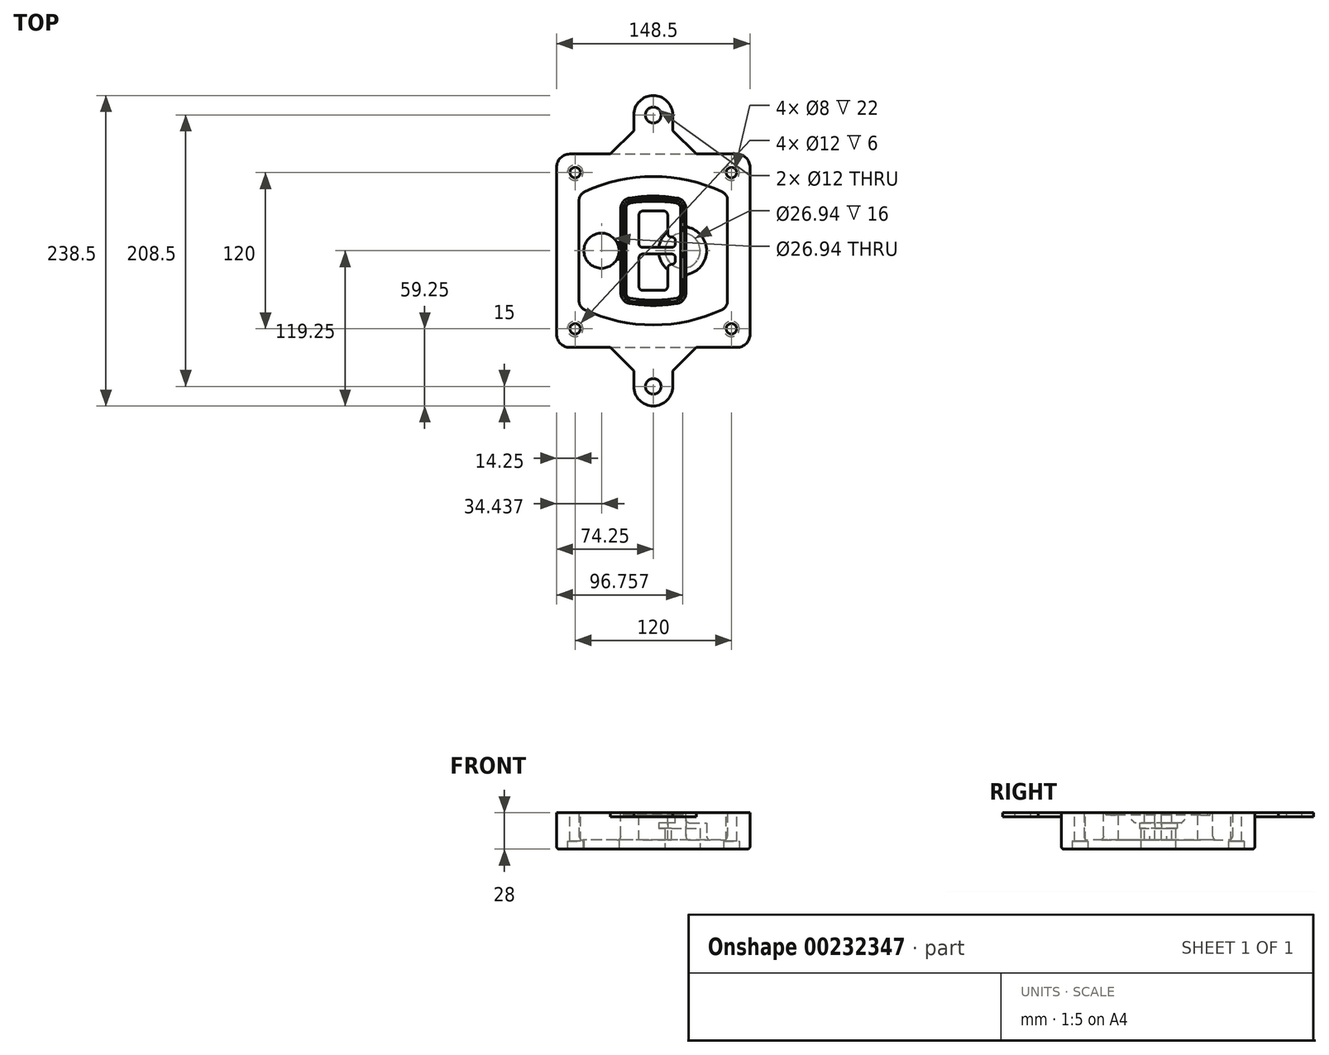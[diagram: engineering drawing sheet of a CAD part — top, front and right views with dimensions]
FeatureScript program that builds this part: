
annotation { "Feature Type Name" : "Feature", "Feature Type Description" : "" }
export const myFeature = defineFeature(function(context is Context, id is Id, definition is map)
    precondition{}
    {
        {
            var Q0;
            Q0=qCreatedBy(makeId("Top.planeOp"),FACE);
            var sketch = newSketch(context, id + "F0", { "sketchPlane" : qUnion([Q0])});
            skPoint(sketch, "E0.rect.middle", {"position": v(0, 0) * mm});
            skLineSegment(sketch, "E1.bottom", {"start": v(-64.25, -74.25) * mm, "end": v(64.25, -74.25) * mm});
            skLineSegment(sketch, "E1.top", {"start": v(-64.25, 74.25) * mm, "end": v(64.25, 74.25) * mm});
            skLineSegment(sketch, "E1.left", {"start": v(-74.25, -64.25) * mm, "end": v(-74.25, 64.25) * mm});
            skLineSegment(sketch, "E1.right", {"start": v(74.25, -64.25) * mm, "end": v(74.25, 64.25) * mm});
            skLineSegment(sketch, "E2", {"start": v(-74.25, 74.25) * mm, "end": v(74.25, -74.25) * mm, "construction": true});
            skLineSegment(sketch, "E3", {"start": v(74.25, 74.25) * mm, "end": v(-74.25, -74.25) * mm, "construction": true});
            skCircle(sketch, "E4", {"center": v(-60, 60) * mm, "radius": 4 * mm});
            skCircle(sketch, "E5", {"center": v(60, 60) * mm, "radius": 4 * mm});
            skCircle(sketch, "E6", {"center": v(60, -60) * mm, "radius": 4 * mm});
            skCircle(sketch, "E7", {"center": v(-60, -60) * mm, "radius": 4 * mm});
            skLineSegment(sketch, "E8", {"start": v(-60, 60) * mm, "end": v(60, 60) * mm, "construction": true});
            skLineSegment(sketch, "E9", {"start": v(60, 60) * mm, "end": v(60, -60) * mm, "construction": true});
            skLineSegment(sketch, "E10", {"start": v(60, -60) * mm, "end": v(-60, -60) * mm, "construction": true});
            skLineSegment(sketch, "E11", {"start": v(-60, -60) * mm, "end": v(-60, 60) * mm, "construction": true});
            skLineSegment(sketch, "E12", {"start": v(-60, 38.83) * mm, "end": v(-60, -38.83) * mm});
            skLineSegment(sketch, "E13", {"start": v(60, 38.83) * mm, "end": v(60, -38.83) * mm});
            skArc(sketch, "E14", {"start": v(54.26, 47.88) * mm, "mid": v(0, 60) * mm, "end": v(-54.26, 47.88) * mm});
            skArc(sketch, "E15", {"start": v(-54.26, -47.88) * mm, "mid": v(0, -60) * mm, "end": v(54.26, -47.88) * mm});
            skLineSegment(sketch, "E16", {"start": v(-60, 0) * mm, "end": v(60, 0) * mm, "construction": true});
            skPoint(sketch, "E17.visualSharp", {"position": v(-60, -45) * mm});
            skArc(sketch, "E17.filletArc", {"start": v(-60, -38.83) * mm, "mid": v(-58.44, -44.2) * mm, "end": v(-54.26, -47.88) * mm});
            skPoint(sketch, "E18.visualSharp", {"position": v(-60, 45) * mm});
            skArc(sketch, "E18.filletArc", {"start": v(-54.26, 47.88) * mm, "mid": v(-58.44, 44.2) * mm, "end": v(-60, 38.83) * mm});
            skPoint(sketch, "E19.visualSharp", {"position": v(60, 45) * mm});
            skArc(sketch, "E19.filletArc", {"start": v(60, 38.83) * mm, "mid": v(58.44, 44.2) * mm, "end": v(54.26, 47.88) * mm});
            skPoint(sketch, "E20.visualSharp", {"position": v(60, -45) * mm});
            skArc(sketch, "E20.filletArc", {"start": v(54.26, -47.88) * mm, "mid": v(58.44, -44.2) * mm, "end": v(60, -38.83) * mm});
            skPoint(sketch, "E21.visualSharp", {"position": v(-74.25, 74.25) * mm});
            skArc(sketch, "E21.filletArc", {"start": v(-64.25, 74.25) * mm, "mid": v(-71.32, 71.32) * mm, "end": v(-74.25, 64.25) * mm});
            skPoint(sketch, "E22.visualSharp", {"position": v(74.25, 74.25) * mm});
            skArc(sketch, "E22.filletArc", {"start": v(74.25, 64.25) * mm, "mid": v(71.32, 71.32) * mm, "end": v(64.25, 74.25) * mm});
            skPoint(sketch, "E23.visualSharp", {"position": v(74.25, -74.25) * mm});
            skArc(sketch, "E23.filletArc", {"start": v(64.25, -74.25) * mm, "mid": v(71.32, -71.32) * mm, "end": v(74.25, -64.25) * mm});
            skPoint(sketch, "E24.visualSharp", {"position": v(-74.25, -74.25) * mm});
            skArc(sketch, "E24.filletArc", {"start": v(-74.25, -64.25) * mm, "mid": v(-71.32, -71.32) * mm, "end": v(-64.25, -74.25) * mm});
            skArc(sketch, "E25.0", {"start": v(57, 38.83) * mm, "mid": v(55.9, 42.58) * mm, "end": v(52.98, 45.17) * mm});
            skLineSegment(sketch, "E25.1", {"start": v(57, 38.83) * mm, "end": v(57, -38.83) * mm});
            skArc(sketch, "E25.2", {"start": v(52.98, -45.17) * mm, "mid": v(55.9, -42.58) * mm, "end": v(57, -38.83) * mm});
            skArc(sketch, "E25.3", {"start": v(-52.98, -45.17) * mm, "mid": v(0, -57) * mm, "end": v(52.98, -45.17) * mm});
            skArc(sketch, "E25.4", {"start": v(-57, -38.83) * mm, "mid": v(-55.9, -42.58) * mm, "end": v(-52.98, -45.17) * mm});
            skArc(sketch, "E25.5", {"start": v(52.98, 45.17) * mm, "mid": v(0, 57) * mm, "end": v(-52.98, 45.17) * mm});
            skLineSegment(sketch, "E25.6", {"start": v(-57, 38.83) * mm, "end": v(-57, -38.83) * mm});
            skArc(sketch, "E25.7", {"start": v(-52.98, 45.17) * mm, "mid": v(-55.9, 42.58) * mm, "end": v(-57, 38.83) * mm});
            skArc(sketch, "E26.0", {"start": v(-55.96, 51.5) * mm, "mid": v(-61.82, 46.33) * mm, "end": v(-64, 38.83) * mm});
            skArc(sketch, "E26.1", {"start": v(55.96, 51.5) * mm, "mid": v(0, 64) * mm, "end": v(-55.96, 51.5) * mm});
            skArc(sketch, "E26.2", {"start": v(64, 38.83) * mm, "mid": v(61.82, 46.33) * mm, "end": v(55.96, 51.5) * mm});
            skLineSegment(sketch, "E26.3", {"start": v(64, 38.83) * mm, "end": v(64, -38.83) * mm});
            skArc(sketch, "E26.4", {"start": v(55.96, -51.5) * mm, "mid": v(61.82, -46.33) * mm, "end": v(64, -38.83) * mm});
            skLineSegment(sketch, "E26.5", {"start": v(-64, 38.83) * mm, "end": v(-64, -38.83) * mm});
            skArc(sketch, "E26.6", {"start": v(-55.96, -51.5) * mm, "mid": v(0, -64) * mm, "end": v(55.96, -51.5) * mm});
            skArc(sketch, "E26.7", {"start": v(-64, -38.83) * mm, "mid": v(-61.82, -46.33) * mm, "end": v(-55.96, -51.5) * mm});
            skSolve(sketch);
        }
        {
            var Q0;
            Q0=makeQuery(id+"F0.imprint","IMPRINT",FACE,{"disambiguationData":[TD([[makeQuery(id+"F0.imprint","IMPRINT",EDGE,{"derivedFrom":sQuery(id+"F0.wireOp",EDGE,"E1.bottom")}),1.0]])]});
            var Q1;
            Q1=makeQuery(id+"F0.imprint","IMPRINT",FACE,{"disambiguationData":[TD([[makeQuery(id+"F0.imprint","IMPRINT",EDGE,{"derivedFrom":sQuery(id+"F0.wireOp",EDGE,"E12")}),1.0]])]});
            var Q2;
            Q2=makeQuery(id+"F0.imprint","IMPRINT",FACE,{"disambiguationData":[TD([[makeQuery(id+"F0.imprint","IMPRINT",EDGE,{"derivedFrom":sQuery(id+"F0.wireOp",EDGE,"E25.0")}),1.0]])]});
            var Q3;
            Q3=makeQuery(id+"F0.imprint","IMPRINT",FACE,{"disambiguationData":[TD([[makeQuery(id+"F0.imprint","IMPRINT",EDGE,{"derivedFrom":sQuery(id+"F0.wireOp",EDGE,"E12")}),-1.0]])]});
            extrude(context, id + "F1", {"entities" : qUnion([Q0, Q1, Q2, Q3]), "oppositeDirection" : true, "depth" : 25 * mm});
        }
        {
            var Q0;
            Q0=makeQuery(id+"F0.imprint","IMPRINT",FACE,{"disambiguationData":[TD([[makeQuery(id+"F0.imprint","IMPRINT",EDGE,{"derivedFrom":sQuery(id+"F0.wireOp",EDGE,"E12")}),1.0]])]});
            extrude(context, id + "F2", {"entities" : qUnion([Q0]), "operationType" : NewBodyOperationType.ADD, "depth" : 3 * mm});
        }
        {
            var Q0;
            Q0=makeQuery(id+"F0.imprint","IMPRINT",FACE,{"disambiguationData":[TD([[makeQuery(id+"F0.imprint","IMPRINT",EDGE,{"derivedFrom":sQuery(id+"F0.wireOp",EDGE,"E25.0")}),1.0]])]});
            extrude(context, id + "F3", {"entities" : qUnion([Q0]), "operationType" : NewBodyOperationType.REMOVE, "oppositeDirection" : true, "depth" : 18 * mm});
        }
        {
            var Q0;
            Q0=makeQuery(id+"F2.opExtrude","CAP_FACE",FACE,{"disambiguationData":[OSD([sQuery(id+"F0.wireOp",EDGE,"E12"),sQuery(id+"F0.wireOp",EDGE,"E13"),sQuery(id+"F0.wireOp",EDGE,"E14"),sQuery(id+"F0.wireOp",EDGE,"E15"),sQuery(id+"F0.wireOp",EDGE,"E17.filletArc"),sQuery(id+"F0.wireOp",EDGE,"E18.filletArc"),sQuery(id+"F0.wireOp",EDGE,"E19.filletArc"),sQuery(id+"F0.wireOp",EDGE,"E20.filletArc"),sQuery(id+"F0.wireOp",EDGE,"E25.0"),sQuery(id+"F0.wireOp",EDGE,"E25.1"),sQuery(id+"F0.wireOp",EDGE,"E25.2"),sQuery(id+"F0.wireOp",EDGE,"E25.3"),sQuery(id+"F0.wireOp",EDGE,"E25.4"),sQuery(id+"F0.wireOp",EDGE,"E25.5"),sQuery(id+"F0.wireOp",EDGE,"E25.6"),sQuery(id+"F0.wireOp",EDGE,"E25.7")])],"isStart":false});
            var sketch = newSketch(context, id + "F4", { "sketchPlane" : qUnion([Q0])});
            skArc(sketch, "E27.0", {"start": v(-18.34, -40.45) * mm, "mid": v(0, -42) * mm, "end": v(18.34, -40.45) * mm});
            skArc(sketch, "E28.0", {"start": v(18.34, 40.45) * mm, "mid": v(0, 42) * mm, "end": v(-18.34, 40.45) * mm});
            skLineSegment(sketch, "E29", {"start": v(-25, 32.57) * mm, "end": v(-25, -32.57) * mm});
            skLineSegment(sketch, "E30", {"start": v(25, 32.57) * mm, "end": v(25, -32.57) * mm});
            skLineSegment(sketch, "E31", {"start": v(-25, 39.1) * mm, "end": v(25, 39.1) * mm, "construction": true});
            skLineSegment(sketch, "E32", {"start": v(-25, -39.1) * mm, "end": v(25, -39.1) * mm, "construction": true});
            skPoint(sketch, "E33.visualSharp", {"position": v(-25, 39.1) * mm});
            skArc(sketch, "E33.filletArc", {"start": v(-18.34, 40.45) * mm, "mid": v(-23.11, 37.73) * mm, "end": v(-25, 32.57) * mm});
            skPoint(sketch, "E34.visualSharp", {"position": v(25, 39.1) * mm});
            skArc(sketch, "E34.filletArc", {"start": v(25, 32.57) * mm, "mid": v(23.11, 37.73) * mm, "end": v(18.34, 40.45) * mm});
            skPoint(sketch, "E35.visualSharp", {"position": v(25, -39.1) * mm});
            skArc(sketch, "E35.filletArc", {"start": v(18.34, -40.45) * mm, "mid": v(23.11, -37.73) * mm, "end": v(25, -32.57) * mm});
            skPoint(sketch, "E36.visualSharp", {"position": v(-25, -39.1) * mm});
            skArc(sketch, "E36.filletArc", {"start": v(-25, -32.57) * mm, "mid": v(-23.11, -37.73) * mm, "end": v(-18.34, -40.45) * mm});
            skArc(sketch, "E37.0", {"start": v(52.98, 45.17) * mm, "mid": v(0, 57) * mm, "end": v(-52.98, 45.17) * mm});
            skArc(sketch, "E37.1", {"start": v(-52.98, 45.17) * mm, "mid": v(-55.9, 42.58) * mm, "end": v(-57, 38.83) * mm});
            skLineSegment(sketch, "E37.2", {"start": v(-57, 38.83) * mm, "end": v(-57, -38.83) * mm});
            skArc(sketch, "E37.3", {"start": v(-57, -38.83) * mm, "mid": v(-55.9, -42.58) * mm, "end": v(-52.98, -45.17) * mm});
            skArc(sketch, "E37.4", {"start": v(-52.98, -45.17) * mm, "mid": v(0, -57) * mm, "end": v(52.98, -45.17) * mm});
            skArc(sketch, "E37.5", {"start": v(52.98, -45.17) * mm, "mid": v(55.9, -42.58) * mm, "end": v(57, -38.83) * mm});
            skLineSegment(sketch, "E37.6", {"start": v(57, 38.83) * mm, "end": v(57, -38.83) * mm});
            skArc(sketch, "E37.7", {"start": v(57, 38.83) * mm, "mid": v(55.9, 42.58) * mm, "end": v(52.98, 45.17) * mm});
            skLineSegment(sketch, "E38.0", {"start": v(23, 32.57) * mm, "end": v(23, -32.57) * mm});
            skArc(sketch, "E38.1", {"start": v(18, -38.48) * mm, "mid": v(21.58, -36.44) * mm, "end": v(23, -32.57) * mm});
            skArc(sketch, "E38.2", {"start": v(-18, -38.48) * mm, "mid": v(0, -40) * mm, "end": v(18, -38.48) * mm});
            skArc(sketch, "E38.3", {"start": v(-23, -32.57) * mm, "mid": v(-21.58, -36.44) * mm, "end": v(-18, -38.48) * mm});
            skLineSegment(sketch, "E38.4", {"start": v(-23, 32.57) * mm, "end": v(-23, -32.57) * mm});
            skArc(sketch, "E38.5", {"start": v(23, 32.57) * mm, "mid": v(21.58, 36.44) * mm, "end": v(18, 38.48) * mm});
            skArc(sketch, "E38.6", {"start": v(-18, 38.48) * mm, "mid": v(-21.58, 36.44) * mm, "end": v(-23, 32.57) * mm});
            skArc(sketch, "E38.7", {"start": v(18, 38.48) * mm, "mid": v(0, 40) * mm, "end": v(-18, 38.48) * mm});
            skArc(sketch, "E39.0", {"start": v(21, 32.57) * mm, "mid": v(20.06, 35.15) * mm, "end": v(17.67, 36.5) * mm});
            skLineSegment(sketch, "E39.1", {"start": v(21, 32.57) * mm, "end": v(21, -32.57) * mm});
            skArc(sketch, "E39.2", {"start": v(17.67, -36.5) * mm, "mid": v(20.06, -35.15) * mm, "end": v(21, -32.57) * mm});
            skArc(sketch, "E39.3", {"start": v(-17.67, -36.5) * mm, "mid": v(0, -38) * mm, "end": v(17.67, -36.5) * mm});
            skArc(sketch, "E39.4", {"start": v(-21, -32.57) * mm, "mid": v(-20.06, -35.15) * mm, "end": v(-17.67, -36.5) * mm});
            skArc(sketch, "E39.5", {"start": v(17.67, 36.5) * mm, "mid": v(0, 38) * mm, "end": v(-17.67, 36.5) * mm});
            skLineSegment(sketch, "E39.6", {"start": v(-21, 32.57) * mm, "end": v(-21, -32.57) * mm});
            skArc(sketch, "E39.7", {"start": v(-17.67, 36.5) * mm, "mid": v(-20.06, 35.15) * mm, "end": v(-21, 32.57) * mm});
            skLineSegment(sketch, "E40", {"start": v(-25, 0) * mm, "end": v(25, 0) * mm, "construction": true});
            skLineSegment(sketch, "E41", {"start": v(-11, 5.5) * mm, "end": v(-11, 27.5) * mm});
            skLineSegment(sketch, "E42", {"start": v(-8, 30.5) * mm, "end": v(8, 30.5) * mm});
            skLineSegment(sketch, "E43", {"start": v(11, 27.5) * mm, "end": v(11, 13.5) * mm});
            skLineSegment(sketch, "E44", {"start": v(14, 10.5) * mm, "end": v(14, 10.5) * mm});
            skLineSegment(sketch, "E45", {"start": v(17, 7.5) * mm, "end": v(17, 5.5) * mm});
            skLineSegment(sketch, "E46", {"start": v(14, 2.5) * mm, "end": v(-8, 2.5) * mm});
            skPoint(sketch, "E47.visualSharp", {"position": v(-11, 30.5) * mm});
            skArc(sketch, "E47.filletArc", {"start": v(-8, 30.5) * mm, "mid": v(-10.12, 29.62) * mm, "end": v(-11, 27.5) * mm});
            skPoint(sketch, "E48.visualSharp", {"position": v(11, 30.5) * mm});
            skArc(sketch, "E48.filletArc", {"start": v(11, 27.5) * mm, "mid": v(10.12, 29.62) * mm, "end": v(8, 30.5) * mm});
            skPoint(sketch, "E49.visualSharp", {"position": v(11, 10.5) * mm});
            skArc(sketch, "E49.filletArc", {"start": v(11, 13.5) * mm, "mid": v(11.88, 11.38) * mm, "end": v(14, 10.5) * mm});
            skPoint(sketch, "E50.visualSharp", {"position": v(17, 10.5) * mm});
            skArc(sketch, "E50.filletArc", {"start": v(17, 7.5) * mm, "mid": v(16.12, 9.62) * mm, "end": v(14, 10.5) * mm});
            skPoint(sketch, "E51.visualSharp", {"position": v(17, 2.5) * mm});
            skArc(sketch, "E51.filletArc", {"start": v(14, 2.5) * mm, "mid": v(16.12, 3.38) * mm, "end": v(17, 5.5) * mm});
            skPoint(sketch, "E52.visualSharp", {"position": v(-11, 2.5) * mm});
            skArc(sketch, "E52.filletArc", {"start": v(-11, 5.5) * mm, "mid": v(-10.12, 3.38) * mm, "end": v(-8, 2.5) * mm});
            skLineSegment(sketch, "E53.0.MirrorCS", {"start": v(14, -2.5) * mm, "end": v(-8, -2.5) * mm});
            skArc(sketch, "E54.0.MirrorCS", {"start": v(-11, -5.5) * mm, "mid": v(-10.12, -3.38) * mm, "end": v(-8, -2.5) * mm});
            skLineSegment(sketch, "E55.0.MirrorCS", {"start": v(-11, -5.5) * mm, "end": v(-11, -27.5) * mm});
            skArc(sketch, "E56.0.MirrorCS", {"start": v(-8, -30.5) * mm, "mid": v(-10.12, -29.62) * mm, "end": v(-11, -27.5) * mm});
            skLineSegment(sketch, "E57.0.MirrorCS", {"start": v(-8, -30.5) * mm, "end": v(8, -30.5) * mm});
            skArc(sketch, "E58.0.MirrorCS", {"start": v(11, -27.5) * mm, "mid": v(10.12, -29.62) * mm, "end": v(8, -30.5) * mm});
            skLineSegment(sketch, "E59.0.MirrorCS", {"start": v(11, -27.5) * mm, "end": v(11, -13.5) * mm});
            skArc(sketch, "E60.0.MirrorCS", {"start": v(11, -13.5) * mm, "mid": v(11.88, -11.38) * mm, "end": v(14, -10.5) * mm});
            skArc(sketch, "E61.0.MirrorCS", {"start": v(17, -7.5) * mm, "mid": v(16.12, -9.62) * mm, "end": v(14, -10.5) * mm});
            skLineSegment(sketch, "E62.0.MirrorCS", {"start": v(17, -7.5) * mm, "end": v(17, -5.5) * mm});
            skArc(sketch, "E63.0.MirrorCS", {"start": v(14, -2.5) * mm, "mid": v(16.12, -3.38) * mm, "end": v(17, -5.5) * mm});
            skSolve(sketch);
        }
        {
            var Q0;
            Q0=makeQuery(id+"F4.imprint","IMPRINT",FACE,{"disambiguationData":[TD([[makeQuery(id+"F4.imprint","IMPRINT",EDGE,{"derivedFrom":sQuery(id+"F4.wireOp",EDGE,"E27.0")}),1.0]])]});
            var Q1;
            Q1=makeQuery(id+"F4.imprint","IMPRINT",FACE,{"disambiguationData":[TD([[makeQuery(id+"F4.imprint","IMPRINT",EDGE,{"derivedFrom":sQuery(id+"F4.wireOp",EDGE,"E38.0")}),-1.0]])]});
            var Q2;
            Q2=makeQuery(id+"F4.imprint","IMPRINT",FACE,{"disambiguationData":[TD([[makeQuery(id+"F4.imprint","IMPRINT",EDGE,{"derivedFrom":sQuery(id+"F4.wireOp",EDGE,"E39.0")}),1.0]])]});
            extrude(context, id + "F5", {"entities" : qUnion([Q0, Q1, Q2]), "operationType" : NewBodyOperationType.ADD, "endBound" : BoundingType.UP_TO_NEXT, "oppositeDirection" : true, "depth" : 25 * mm});
        }
        {
            var Q0;
            Q0=makeQuery(id+"F4.imprint","IMPRINT",FACE,{"disambiguationData":[TD([[makeQuery(id+"F4.imprint","IMPRINT",EDGE,{"derivedFrom":sQuery(id+"F4.wireOp",EDGE,"E38.0")}),-1.0]])]});
            extrude(context, id + "F6", {"entities" : qUnion([Q0]), "operationType" : NewBodyOperationType.REMOVE, "oppositeDirection" : true, "depth" : 2 * mm});
        }
        {
            var Q0;
            Q0=makeQuery(id+"F1.opExtrude","CAP_FACE",FACE,{"disambiguationData":[OSD([sQuery(id+"F0.wireOp",EDGE,"E1.bottom"),sQuery(id+"F0.wireOp",EDGE,"E1.top"),sQuery(id+"F0.wireOp",EDGE,"E1.left"),sQuery(id+"F0.wireOp",EDGE,"E1.right"),sQuery(id+"F0.wireOp",EDGE,"E4"),sQuery(id+"F0.wireOp",EDGE,"E5"),sQuery(id+"F0.wireOp",EDGE,"E6"),sQuery(id+"F0.wireOp",EDGE,"E7"),sQuery(id+"F0.wireOp",EDGE,"E21.filletArc"),sQuery(id+"F0.wireOp",EDGE,"E22.filletArc"),sQuery(id+"F0.wireOp",EDGE,"E23.filletArc"),sQuery(id+"F0.wireOp",EDGE,"E24.filletArc")])],"isStart":false});
            var sketch = newSketch(context, id + "F7", { "sketchPlane" : qUnion([Q0])});
            skCircle(sketch, "E64", {"center": v(22.5, 0) * mm, "radius": 13.47 * mm});
            skCircle(sketch, "E65", {"center": v(-39.81, 0) * mm, "radius": 13.47 * mm});
            skLineSegment(sketch, "E66", {"start": v(74.25, 0) * mm, "end": v(-74.25, 0) * mm});
            skCircle(sketch, "E67", {"center": v(22.5, 0) * mm, "radius": 18.47 * mm});
            skCircle(sketch, "E68", {"center": v(60, -60) * mm, "radius": 6 * mm});
            skCircle(sketch, "E69", {"center": v(-60, -60) * mm, "radius": 6 * mm});
            skCircle(sketch, "E70", {"center": v(-60, 60) * mm, "radius": 6 * mm});
            skCircle(sketch, "E71", {"center": v(60, 60) * mm, "radius": 6 * mm});
            skSolve(sketch);
        }
        {
            var Q0;
            {var subQ1=sQuery(id+"F7.wireOp",EDGE,"E66");var subQ4=sQuery(id+"F7.wireOp",EDGE,"E64");var subQ6=makeQuery(id+"F7.imprint","INTERSECT",VERTEX,{"disambiguationData":[OD(0.0)],"derivedFrom":[subQ4,subQ1]});Q0=makeQuery(id+"F7.imprint","IMPRINT",FACE,{"disambiguationData":[TD([[makeQuery(id+"F7.imprint","IMPRINT",EDGE,{"disambiguationData":[TD([[subQ6,-1.0]])],"derivedFrom":subQ4}),-1.0]])]});}
            var Q1;
            {var subQ0=sQuery(id+"F7.wireOp",EDGE,"E66");var subQ1=sQuery(id+"F7.wireOp",EDGE,"E64");var subQ3=makeQuery(id+"F7.imprint","INTERSECT",VERTEX,{"disambiguationData":[OD(0.0)],"derivedFrom":[subQ1,subQ0]});Q1=makeQuery(id+"F7.imprint","IMPRINT",FACE,{"disambiguationData":[TD([[makeQuery(id+"F7.imprint","IMPRINT",EDGE,{"disambiguationData":[TD([[subQ3,-1.0]])],"derivedFrom":subQ1}),1.0]])]});}
            var Q2;
            {var subQ0=sQuery(id+"F7.wireOp",EDGE,"E66");var subQ1=sQuery(id+"F7.wireOp",EDGE,"E64");var subQ3=makeQuery(id+"F7.imprint","INTERSECT",VERTEX,{"disambiguationData":[OD(0.0)],"derivedFrom":[subQ1,subQ0]});Q2=makeQuery(id+"F7.imprint","IMPRINT",FACE,{"disambiguationData":[TD([[makeQuery(id+"F7.imprint","IMPRINT",EDGE,{"disambiguationData":[TD([[subQ3,1.0]])],"derivedFrom":subQ1}),1.0]])]});}
            var Q3;
            {var subQ1=sQuery(id+"F7.wireOp",EDGE,"E66");var subQ4=sQuery(id+"F7.wireOp",EDGE,"E64");var subQ6=makeQuery(id+"F7.imprint","INTERSECT",VERTEX,{"disambiguationData":[OD(0.0)],"derivedFrom":[subQ4,subQ1]});Q3=makeQuery(id+"F7.imprint","IMPRINT",FACE,{"disambiguationData":[TD([[makeQuery(id+"F7.imprint","IMPRINT",EDGE,{"disambiguationData":[TD([[subQ6,1.0]])],"derivedFrom":subQ4}),-1.0]])]});}
            extrude(context, id + "F8", {"entities" : qUnion([Q0, Q1, Q2, Q3]), "operationType" : NewBodyOperationType.ADD, "oppositeDirection" : true, "depth" : 20 * mm});
        }
        {
            var Q0;
            {var subQ0=sQuery(id+"F7.wireOp",EDGE,"E66");var subQ1=sQuery(id+"F7.wireOp",EDGE,"E64");var subQ3=makeQuery(id+"F7.imprint","INTERSECT",VERTEX,{"disambiguationData":[OD(0.0)],"derivedFrom":[subQ1,subQ0]});Q0=makeQuery(id+"F7.imprint","IMPRINT",FACE,{"disambiguationData":[TD([[makeQuery(id+"F7.imprint","IMPRINT",EDGE,{"disambiguationData":[TD([[subQ3,-1.0]])],"derivedFrom":subQ1}),1.0]])]});}
            var Q1;
            {var subQ0=sQuery(id+"F7.wireOp",EDGE,"E66");var subQ1=sQuery(id+"F7.wireOp",EDGE,"E64");var subQ3=makeQuery(id+"F7.imprint","INTERSECT",VERTEX,{"disambiguationData":[OD(0.0)],"derivedFrom":[subQ1,subQ0]});Q1=makeQuery(id+"F7.imprint","IMPRINT",FACE,{"disambiguationData":[TD([[makeQuery(id+"F7.imprint","IMPRINT",EDGE,{"disambiguationData":[TD([[subQ3,1.0]])],"derivedFrom":subQ1}),1.0]])]});}
            extrude(context, id + "F9", {"entities" : qUnion([Q0, Q1]), "operationType" : NewBodyOperationType.REMOVE, "oppositeDirection" : true, "depth" : 16 * mm});
        }
        {
            var Q0;
            {var subQ0=sQuery(id+"F7.wireOp",EDGE,"E66");var subQ1=sQuery(id+"F7.wireOp",EDGE,"E65");var subQ3=makeQuery(id+"F7.imprint","INTERSECT",VERTEX,{"disambiguationData":[OD(0.0)],"derivedFrom":[subQ1,subQ0]});Q0=makeQuery(id+"F7.imprint","IMPRINT",FACE,{"disambiguationData":[TD([[makeQuery(id+"F7.imprint","IMPRINT",EDGE,{"disambiguationData":[TD([[subQ3,-1.0]])],"derivedFrom":subQ1}),1.0]])]});}
            var Q1;
            {var subQ0=sQuery(id+"F7.wireOp",EDGE,"E66");var subQ1=sQuery(id+"F7.wireOp",EDGE,"E65");var subQ3=makeQuery(id+"F7.imprint","INTERSECT",VERTEX,{"disambiguationData":[OD(0.0)],"derivedFrom":[subQ1,subQ0]});Q1=makeQuery(id+"F7.imprint","IMPRINT",FACE,{"disambiguationData":[TD([[makeQuery(id+"F7.imprint","IMPRINT",EDGE,{"disambiguationData":[TD([[subQ3,1.0]])],"derivedFrom":subQ1}),1.0]])]});}
            extrude(context, id + "F10", {"entities" : qUnion([Q0, Q1]), "operationType" : NewBodyOperationType.REMOVE, "oppositeDirection" : true, "depth" : 25 * mm});
        }
        {
            var Q0;
            Q0=makeQuery(id+"F7.imprint","IMPRINT",FACE,{"disambiguationData":[TD([[makeQuery(id+"F7.imprint","IMPRINT",EDGE,{"derivedFrom":sQuery(id+"F7.wireOp",EDGE,"E68")}),1.0]])]});
            var Q1;
            Q1=makeQuery(id+"F7.imprint","IMPRINT",FACE,{"disambiguationData":[TD([[makeQuery(id+"F7.imprint","IMPRINT",EDGE,{"derivedFrom":makeQuery(id+"F1.opExtrude","CAP_EDGE",EDGE,{"disambiguationData":[OSD([sQuery(id+"F0.wireOp",EDGE,"E5")])],"isStart":false})}),-1.0]])]});
            var Q2;
            Q2=makeQuery(id+"F7.imprint","IMPRINT",FACE,{"disambiguationData":[TD([[makeQuery(id+"F7.imprint","IMPRINT",EDGE,{"derivedFrom":sQuery(id+"F7.wireOp",EDGE,"E69")}),1.0]])]});
            var Q3;
            Q3=makeQuery(id+"F7.imprint","IMPRINT",FACE,{"disambiguationData":[TD([[makeQuery(id+"F7.imprint","IMPRINT",EDGE,{"derivedFrom":makeQuery(id+"F1.opExtrude","CAP_EDGE",EDGE,{"disambiguationData":[OSD([sQuery(id+"F0.wireOp",EDGE,"E4")])],"isStart":false})}),-1.0]])]});
            var Q4;
            Q4=makeQuery(id+"F7.imprint","IMPRINT",FACE,{"disambiguationData":[TD([[makeQuery(id+"F7.imprint","IMPRINT",EDGE,{"derivedFrom":sQuery(id+"F7.wireOp",EDGE,"E70")}),1.0]])]});
            var Q5;
            Q5=makeQuery(id+"F7.imprint","IMPRINT",FACE,{"disambiguationData":[TD([[makeQuery(id+"F7.imprint","IMPRINT",EDGE,{"derivedFrom":makeQuery(id+"F1.opExtrude","CAP_EDGE",EDGE,{"disambiguationData":[OSD([sQuery(id+"F0.wireOp",EDGE,"E7")])],"isStart":false})}),-1.0]])]});
            var Q6;
            Q6=makeQuery(id+"F7.imprint","IMPRINT",FACE,{"disambiguationData":[TD([[makeQuery(id+"F7.imprint","IMPRINT",EDGE,{"derivedFrom":sQuery(id+"F7.wireOp",EDGE,"E71")}),1.0]])]});
            var Q7;
            Q7=makeQuery(id+"F7.imprint","IMPRINT",FACE,{"disambiguationData":[TD([[makeQuery(id+"F7.imprint","IMPRINT",EDGE,{"derivedFrom":makeQuery(id+"F1.opExtrude","CAP_EDGE",EDGE,{"disambiguationData":[OSD([sQuery(id+"F0.wireOp",EDGE,"E6")])],"isStart":false})}),-1.0]])]});
            extrude(context, id + "F11", {"entities" : qUnion([Q0, Q1, Q2, Q3, Q4, Q5, Q6, Q7]), "operationType" : NewBodyOperationType.REMOVE, "oppositeDirection" : true, "depth" : 6 * mm});
        }
        {
            var Q0;
            Q0=makeQuery(id+"F9.boolean.opBoolean","COPY",FACE,{"derivedFrom":makeQuery(id+"F9.opExtrude","CAP_FACE",FACE,{"disambiguationData":[OSD([sQuery(id+"F7.wireOp",EDGE,"E64")])],"isStart":false})});
            var sketch = newSketch(context, id + "F12", { "sketchPlane" : qUnion([Q0])});
            skArc(sketch, "E72.0", {"start": v(11, 14.45) * mm, "mid": v(6.45, 9.13) * mm, "end": v(4.2, 2.5) * mm});
            skArc(sketch, "E72.1", {"start": v(4.2, -2.5) * mm, "mid": v(6.45, -9.13) * mm, "end": v(11, -14.45) * mm});
            skLineSegment(sketch, "E73", {"start": v(4.2, -2.5) * mm, "end": v(14, -2.5) * mm});
            skLineSegment(sketch, "E74.0", {"start": v(14, 2.5) * mm, "end": v(4.2, 2.5) * mm});
            skArc(sketch, "E74.1", {"start": v(14, 2.5) * mm, "mid": v(16.12, 3.38) * mm, "end": v(17, 5.5) * mm});
            skLineSegment(sketch, "E74.2", {"start": v(17, 7.5) * mm, "end": v(17, 5.5) * mm});
            skArc(sketch, "E74.3", {"start": v(17, 7.5) * mm, "mid": v(16.12, 9.62) * mm, "end": v(14, 10.5) * mm});
            skArc(sketch, "E74.4", {"start": v(11, 13.5) * mm, "mid": v(11.88, 11.38) * mm, "end": v(14, 10.5) * mm});
            skLineSegment(sketch, "E74.5", {"start": v(11, 14.45) * mm, "end": v(11, 13.5) * mm});
            skLineSegment(sketch, "E74.7", {"start": v(14, -2.5) * mm, "end": v(4.2, -2.5) * mm});
            skArc(sketch, "E74.8", {"start": v(14, -2.5) * mm, "mid": v(16.12, -3.38) * mm, "end": v(17, -5.5) * mm});
            skLineSegment(sketch, "E74.9", {"start": v(17, -7.5) * mm, "end": v(17, -5.5) * mm});
            skArc(sketch, "E74.10", {"start": v(17, -7.5) * mm, "mid": v(16.12, -9.62) * mm, "end": v(14, -10.5) * mm});
            skArc(sketch, "E74.11", {"start": v(11, -13.5) * mm, "mid": v(11.88, -11.38) * mm, "end": v(14, -10.5) * mm});
            skLineSegment(sketch, "E74.12", {"start": v(11, -14.45) * mm, "end": v(11, -13.5) * mm});
            skPoint(sketch, "E75.orphan", {"position": v(11, -27.5) * mm});
            skPoint(sketch, "E76.orphan", {"position": v(-8, -2.5) * mm});
            skPoint(sketch, "E77.orphan", {"position": v(-8, 2.5) * mm});
            skPoint(sketch, "E78.orphan", {"position": v(11, 27.5) * mm});
            skSolve(sketch);
        }
        {
            var Q0;
            {var subQ7=sQuery(id+"F12.wireOp",EDGE,"E72.0");var subQ14=sQuery(id+"F12.wireOp",EDGE,"E72.1");var subQ16=sQuery(id+"F12.wireOp",EDGE,"E74.1");var subQ18=sQuery(id+"F12.wireOp",EDGE,"E74.8");Q0=qUnion([makeQuery(id+"F12.imprint","IMPRINT",FACE,{"disambiguationData":[TD([[makeQuery(id+"F12.imprint","IMPRINT",EDGE,{"derivedFrom":subQ7}),1.0]])]}),makeQuery(id+"F12.imprint","IMPRINT",FACE,{"disambiguationData":[TD([[makeQuery(id+"F12.imprint","IMPRINT",EDGE,{"derivedFrom":subQ14}),1.0]])]}),makeQuery(id+"F12.imprint","IMPRINT",FACE,{"disambiguationData":[TD([[makeQuery(id+"F12.imprint","IMPRINT",EDGE,{"derivedFrom":subQ16}),1.0]])]}),makeQuery(id+"F12.imprint","IMPRINT",FACE,{"disambiguationData":[TD([[makeQuery(id+"F12.imprint","IMPRINT",EDGE,{"derivedFrom":subQ18}),-1.0]])]})]);}
            var Q1;
            Q1=makeQuery(id+"F5.boolean.opBoolean","SPLIT",FACE,{"disambiguationData":[TD([makeQuery(id+"F5.opExtrude","SWEPT_FACE",FACE,{"disambiguationData":[OSD([sQuery(id+"F4.wireOp",EDGE,"E41")])]})])],"derivedFrom":makeQuery(id+"F3.boolean.opBoolean","COPY",FACE,{"derivedFrom":makeQuery(id+"F3.opExtrude","CAP_FACE",FACE,{"disambiguationData":[OSD([sQuery(id+"F0.wireOp",EDGE,"E25.0"),sQuery(id+"F0.wireOp",EDGE,"E25.1"),sQuery(id+"F0.wireOp",EDGE,"E25.2"),sQuery(id+"F0.wireOp",EDGE,"E25.3"),sQuery(id+"F0.wireOp",EDGE,"E25.4"),sQuery(id+"F0.wireOp",EDGE,"E25.5"),sQuery(id+"F0.wireOp",EDGE,"E25.6"),sQuery(id+"F0.wireOp",EDGE,"E25.7")])],"isStart":false})})});
            extrude(context, id + "F13", {"entities" : qUnion([Q0]), "operationType" : NewBodyOperationType.REMOVE, "endBound" : BoundingType.UP_TO_SURFACE, "endBoundEntityFace" : qUnion([Q1]), "depth" : 25 * mm});
        }
        {
            var Q0;
            Q0=makeQuery(id+"F3.boolean.opBoolean","COPY",EDGE,{"derivedFrom":makeQuery(id+"F3.opExtrude","CAP_EDGE",EDGE,{"disambiguationData":[OSD([sQuery(id+"F0.wireOp",EDGE,"E25.6")])],"isStart":false})});
            var Q1;
            Q1=makeQuery(id+"F8.boolean.opBoolean","INTERSECT",EDGE,{"derivedFrom":[makeQuery(id+"F5.opExtrude","SWEPT_FACE",FACE,{"disambiguationData":[OSD([sQuery(id+"F4.wireOp",EDGE,"E30")])]}),makeQuery(id+"F8.opExtrude","CAP_FACE",FACE,{"disambiguationData":[OSD([sQuery(id+"F7.wireOp",EDGE,"E67")])],"isStart":false})]});
            var Q2;
            Q2=makeQuery(id+"F8.boolean.opBoolean","INTERSECT",EDGE,{"disambiguationData":[OD(1.0)],"derivedFrom":[makeQuery(id+"F5.opExtrude","SWEPT_FACE",FACE,{"disambiguationData":[OSD([sQuery(id+"F4.wireOp",EDGE,"E30")])]}),makeQuery(id+"F8.opExtrude","SWEPT_FACE",FACE,{"disambiguationData":[OSD([sQuery(id+"F7.wireOp",EDGE,"E67")])]})]});
            var Q3;
            {var subQ0=sQuery(id+"F4.wireOp",EDGE,"E30");Q3=makeQuery(id+"F8.boolean.opBoolean","SPLIT",EDGE,{"disambiguationData":[TD([makeQuery(id+"F5.opExtrude","SWEPT_FACE",FACE,{"disambiguationData":[OSD([sQuery(id+"F4.wireOp",EDGE,"E35.filletArc")])]})])],"derivedFrom":makeQuery(id+"F5.opExtrude","CAP_EDGE",EDGE,{"disambiguationData":[OSD([subQ0])],"isStart":false})});}
            var Q4;
            {var subQ0=sQuery(id+"F0.wireOp",EDGE,"E25.7");var subQ1=sQuery(id+"F0.wireOp",EDGE,"E25.1");var subQ2=sQuery(id+"F0.wireOp",EDGE,"E25.6");var subQ3=sQuery(id+"F0.wireOp",EDGE,"E25.5");var subQ4=sQuery(id+"F0.wireOp",EDGE,"E25.4");var subQ5=sQuery(id+"F0.wireOp",EDGE,"E25.0");var subQ6=sQuery(id+"F0.wireOp",EDGE,"E25.2");var subQ7=sQuery(id+"F0.wireOp",EDGE,"E25.3");Q4=makeQuery(id+"F8.boolean.opBoolean","INTERSECT",EDGE,{"derivedFrom":[makeQuery(id+"F5.boolean.opBoolean","SPLIT",FACE,{"disambiguationData":[TD([makeQuery(id+"F2.opExtrude","SWEPT_FACE",FACE,{"disambiguationData":[OSD([subQ5])]})])],"derivedFrom":makeQuery(id+"F3.boolean.opBoolean","COPY",FACE,{"derivedFrom":makeQuery(id+"F3.opExtrude","CAP_FACE",FACE,{"disambiguationData":[OSD([subQ5,subQ1,subQ6,subQ7,subQ4,subQ3,subQ2,subQ0])],"isStart":false})})}),makeQuery(id+"F8.opExtrude","SWEPT_FACE",FACE,{"disambiguationData":[OSD([sQuery(id+"F7.wireOp",EDGE,"E67")])]})]});}
            var Q5;
            Q5=makeQuery(id+"F8.boolean.opBoolean","INTERSECT",EDGE,{"disambiguationData":[OD(0.0)],"derivedFrom":[makeQuery(id+"F5.opExtrude","SWEPT_FACE",FACE,{"disambiguationData":[OSD([sQuery(id+"F4.wireOp",EDGE,"E30")])]}),makeQuery(id+"F8.opExtrude","SWEPT_FACE",FACE,{"disambiguationData":[OSD([sQuery(id+"F7.wireOp",EDGE,"E67")])]})]});
            fillet(context, id + "F14", {"entities" : qUnion([Q0, Q1, Q2, Q3, Q4, Q5]), "radius" : 3 * mm, "tangentPropagation" : true, "allowEdgeOverflow" : false});
        }
        {
            var Q0;
            Q0=makeQuery(id+"F1.opExtrude","CAP_EDGE",EDGE,{"disambiguationData":[OSD([sQuery(id+"F0.wireOp",EDGE,"E1.bottom")])],"isStart":false});
            fillet(context, id + "F15", {"entities" : qUnion([Q0]), "radius" : 2 * mm, "tangentPropagation" : true, "allowEdgeOverflow" : false});
        }
        {
            var Q0;
            {var subQ0=sQuery(id+"F0.wireOp",EDGE,"E22.filletArc");var subQ1=sQuery(id+"F0.wireOp",EDGE,"E7");var subQ2=sQuery(id+"F0.wireOp",EDGE,"E6");var subQ3=sQuery(id+"F0.wireOp",EDGE,"E5");var subQ4=sQuery(id+"F0.wireOp",EDGE,"E4");var subQ5=sQuery(id+"F0.wireOp",EDGE,"E1.bottom");var subQ6=sQuery(id+"F0.wireOp",EDGE,"E21.filletArc");var subQ7=sQuery(id+"F0.wireOp",EDGE,"E1.top");var subQ8=sQuery(id+"F0.wireOp",EDGE,"E1.left");var subQ9=sQuery(id+"F0.wireOp",EDGE,"E1.right");var subQ10=sQuery(id+"F0.wireOp",EDGE,"E23.filletArc");var subQ11=sQuery(id+"F0.wireOp",EDGE,"E24.filletArc");Q0=makeQuery(id+"F2.boolean.opBoolean","SPLIT",FACE,{"disambiguationData":[TD([makeQuery(id+"F1.opExtrude","SWEPT_FACE",FACE,{"disambiguationData":[OSD([subQ5])]})])],"derivedFrom":makeQuery(id+"F1.opExtrude","CAP_FACE",FACE,{"disambiguationData":[OSD([subQ5,subQ7,subQ8,subQ9,subQ4,subQ3,subQ2,subQ1,subQ6,subQ0,subQ10,subQ11])],"isStart":true})});}
            var sketch = newSketch(context, id + "F16", { "sketchPlane" : qUnion([Q0])});
            skLineSegment(sketch, "E79.0", {"start": v(-74.25, -64.25) * mm, "end": v(-74.25, 64.25) * mm});
            skArc(sketch, "E79.1", {"start": v(-64.25, 74.25) * mm, "mid": v(-71.32, 71.32) * mm, "end": v(-74.25, 64.25) * mm});
            skLineSegment(sketch, "E79.2", {"start": v(-64.25, 74.25) * mm, "end": v(64.25, 74.25) * mm});
            skArc(sketch, "E79.3", {"start": v(74.25, 64.25) * mm, "mid": v(71.32, 71.32) * mm, "end": v(64.25, 74.25) * mm});
            skLineSegment(sketch, "E79.4", {"start": v(74.25, -64.25) * mm, "end": v(74.25, 64.25) * mm});
            skCircle(sketch, "E79.5", {"center": v(60, 60) * mm, "radius": 4 * mm});
            skCircle(sketch, "E79.6", {"center": v(-60, 60) * mm, "radius": 4 * mm});
            skCircle(sketch, "E79.7", {"center": v(-60, -60) * mm, "radius": 4 * mm});
            skCircle(sketch, "E79.8", {"center": v(60, -60) * mm, "radius": 4 * mm});
            skArc(sketch, "E79.9", {"start": v(-54.26, -47.88) * mm, "mid": v(0, -60) * mm, "end": v(54.26, -47.88) * mm});
            skArc(sketch, "E79.10", {"start": v(54.26, -47.88) * mm, "mid": v(58.44, -44.2) * mm, "end": v(60, -38.83) * mm});
            skLineSegment(sketch, "E79.11", {"start": v(60, 38.83) * mm, "end": v(60, -38.83) * mm});
            skArc(sketch, "E79.12", {"start": v(60, 38.83) * mm, "mid": v(58.44, 44.2) * mm, "end": v(54.26, 47.88) * mm});
            skArc(sketch, "E79.13", {"start": v(54.26, 47.88) * mm, "mid": v(0, 60) * mm, "end": v(-54.26, 47.88) * mm});
            skArc(sketch, "E79.14", {"start": v(-54.26, 47.88) * mm, "mid": v(-58.44, 44.2) * mm, "end": v(-60, 38.83) * mm});
            skLineSegment(sketch, "E79.15", {"start": v(-60, 38.83) * mm, "end": v(-60, -38.83) * mm});
            skArc(sketch, "E79.16", {"start": v(-60, -38.83) * mm, "mid": v(-58.44, -44.2) * mm, "end": v(-54.26, -47.88) * mm});
            skArc(sketch, "E79.17", {"start": v(-74.25, -64.25) * mm, "mid": v(-71.32, -71.32) * mm, "end": v(-64.25, -74.25) * mm});
            skLineSegment(sketch, "E79.18", {"start": v(-64.25, -74.25) * mm, "end": v(64.25, -74.25) * mm});
            skArc(sketch, "E79.19", {"start": v(64.25, -74.25) * mm, "mid": v(71.32, -71.32) * mm, "end": v(74.25, -64.25) * mm});
            skLineSegment(sketch, "E80", {"start": v(0, 74.25) * mm, "end": v(0, 104.25) * mm});
            skCircle(sketch, "E81", {"center": v(0, 104.25) * mm, "radius": 6 * mm});
            skLineSegment(sketch, "E82", {"start": v(-33, 74.25) * mm, "end": v(-15, 92.25) * mm});
            skLineSegment(sketch, "E83", {"start": v(33, 74.25) * mm, "end": v(15, 92.25) * mm});
            skLineSegment(sketch, "E84", {"start": v(-15, 92.25) * mm, "end": v(-15, 104.25) * mm});
            skLineSegment(sketch, "E85", {"start": v(15, 92.25) * mm, "end": v(15, 104.25) * mm});
            skArc(sketch, "E86", {"start": v(15, 104.25) * mm, "mid": v(0, 119.25) * mm, "end": v(-15, 104.25) * mm});
            skLineSegment(sketch, "E87", {"start": v(-74.25, 0) * mm, "end": v(74.25, 0) * mm, "construction": true});
            skLineSegment(sketch, "E88.MirrorCS", {"start": v(-33, -74.25) * mm, "end": v(-15, -92.25) * mm});
            skLineSegment(sketch, "E89.MirrorCS", {"start": v(-15, -92.25) * mm, "end": v(-15, -104.25) * mm});
            skArc(sketch, "E90.MirrorCS", {"start": v(15, -104.25) * mm, "mid": v(0, -119.25) * mm, "end": v(-15, -104.25) * mm});
            skLineSegment(sketch, "E91.MirrorCS", {"start": v(15, -92.25) * mm, "end": v(15, -104.25) * mm});
            skCircle(sketch, "E92.MirrorC", {"center": v(0, -104.25) * mm, "radius": 6 * mm});
            skLineSegment(sketch, "E93.MirrorCS", {"start": v(33, -74.25) * mm, "end": v(15, -92.25) * mm});
            skLineSegment(sketch, "E94.MirrorCS", {"start": v(0, -74.25) * mm, "end": v(0, -104.25) * mm});
            skSolve(sketch);
        }
        {
            var Q0;
            Q0=makeQuery(id+"F16.imprint","IMPRINT",FACE,{"disambiguationData":[TD([[makeQuery(id+"F16.imprint","IMPRINT",EDGE,{"derivedFrom":sQuery(id+"F16.wireOp",EDGE,"E81")}),-1.0]])]});
            var Q1;
            Q1=makeQuery(id+"F16.imprint","IMPRINT",FACE,{"disambiguationData":[TD([[makeQuery(id+"F16.imprint","IMPRINT",EDGE,{"derivedFrom":sQuery(id+"F16.wireOp",EDGE,"E79.0")}),-1.0]])]});
            var Q2;
            {var subQ0=sQuery(id+"F16.wireOp",EDGE,"E88.MirrorCS");Q2=makeQuery(id+"F16.imprint","IMPRINT",FACE,{"disambiguationData":[TD([[makeQuery(id+"F16.imprint","IMPRINT",EDGE,{"derivedFrom":subQ0}),1.0]])]});}
            var Q3;
            Q3=makeQuery(id+"F2.opExtrude","CAP_FACE",FACE,{"disambiguationData":[OSD([sQuery(id+"F0.wireOp",EDGE,"E12"),sQuery(id+"F0.wireOp",EDGE,"E13"),sQuery(id+"F0.wireOp",EDGE,"E14"),sQuery(id+"F0.wireOp",EDGE,"E15"),sQuery(id+"F0.wireOp",EDGE,"E17.filletArc"),sQuery(id+"F0.wireOp",EDGE,"E18.filletArc"),sQuery(id+"F0.wireOp",EDGE,"E19.filletArc"),sQuery(id+"F0.wireOp",EDGE,"E20.filletArc"),sQuery(id+"F0.wireOp",EDGE,"E25.0"),sQuery(id+"F0.wireOp",EDGE,"E25.1"),sQuery(id+"F0.wireOp",EDGE,"E25.2"),sQuery(id+"F0.wireOp",EDGE,"E25.3"),sQuery(id+"F0.wireOp",EDGE,"E25.4"),sQuery(id+"F0.wireOp",EDGE,"E25.5"),sQuery(id+"F0.wireOp",EDGE,"E25.6"),sQuery(id+"F0.wireOp",EDGE,"E25.7")])],"isStart":false});
            extrude(context, id + "F17", {"entities" : qUnion([Q0, Q1, Q2]), "operationType" : NewBodyOperationType.ADD, "endBound" : BoundingType.UP_TO_SURFACE, "endBoundEntityFace" : qUnion([Q3]), "depth" : 25 * mm});
        }
    });
